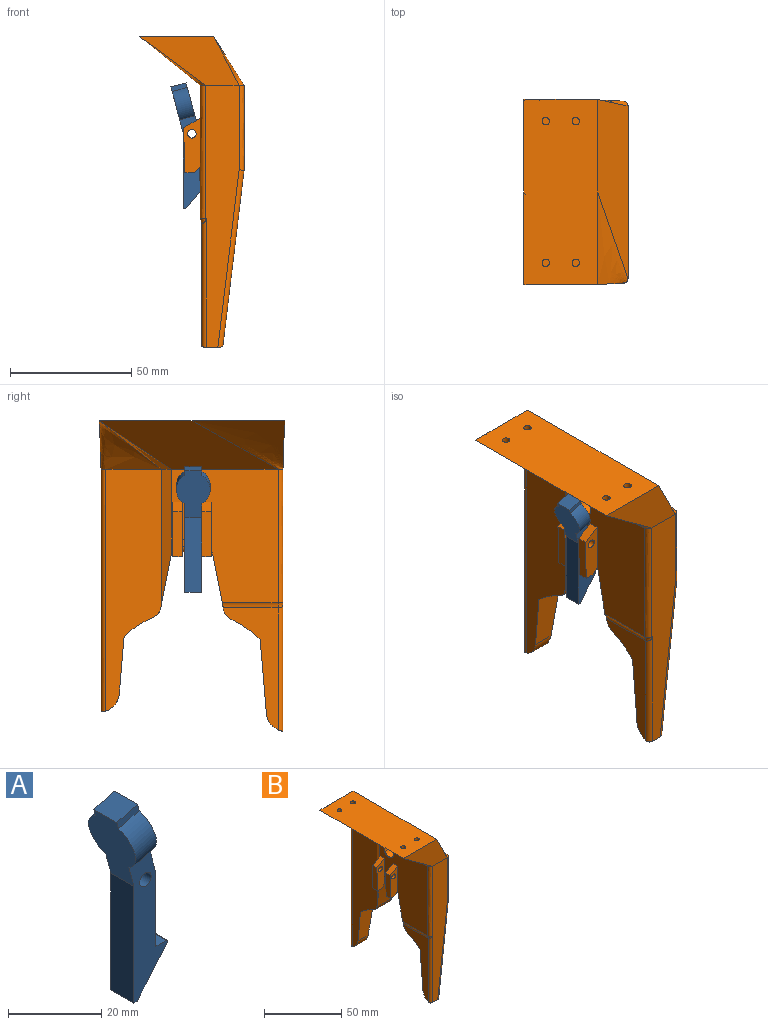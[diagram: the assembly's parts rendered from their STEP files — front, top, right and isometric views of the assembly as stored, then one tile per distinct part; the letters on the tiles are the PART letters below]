
ASSEMBLY  parts=2 mates=1
PART A: 18 faces, bbox 15.4x14x51.8 mm
  f0: plane 6.78x3.55mm, normal (0,-1,0), area 12.6mm2, adj f2,f3,f4,f14
  f1: plane 6.78x3.55mm, normal (0,1,0), area 12.6mm2, adj f2,f3,f4,f13
  f2: plane 20.89x14mm, normal (0.97,0,0.26), area 153.5mm2, adj f0,f1,f3,f9,f11,f12,f13,f14
  f3: plane 7x6.28mm, normal (-0.26,0,0.97), area 45.5mm2, adj f0,f1,f2,f4
  f4: plane 19.32x14mm, normal (-0.97,0,-0.26), area 200.2mm2, adj f0,f1,f3,f5,f11,f12,f13,f14
  f5: plane 30.76x7mm, normal (-1,0,0), area 215.3mm2, adj f4,f6,f11,f12
  f6: plane 7x1mm, normal (0,0,-1), area 7mm2, adj f5,f7,f11,f12
  f7: plane 10.9x9.15mm, normal (0.77,0,-0.64), area 99.6mm2, adj f6,f11,f12,f17
  f8: plane 7x3.14mm, normal (0,0,1), area 22mm2, adj f9,f11,f12,f17
  f9: plane 19.31x7mm, normal (1,0,0), area 135.2mm2, adj f2,f8,f11,f12
  f10: cylinder r=1.75mm len=7mm, axis (0,1,0), area 77mm2, adj f11,f12
  f11: plane 38.18x11.78mm, normal (0,-1,0), area 230.7mm2, adj f2,f4,f5,f6,f7,f8,f9,f10
  f12: plane 38.18x11.78mm, normal (0,1,0), area 230.7mm2, adj f2,f4,f5,f6,f7,f8,f9,f10
  f13: cylinder r=7mm len=13.39mm, axis (-0.97,0,-0.26), area 95.3mm2, adj f1,f2,f4,f12
  f14: cylinder r=7mm len=13.39mm, axis (-0.97,0,-0.26), area 95.3mm2, adj f0,f2,f4,f11
  f15: cylinder r=4.3mm len=9.68mm, axis (0.97,0,0.26), area 143.2mm2, adj f2,f16
  f16: plane 8.6x8.31mm, normal (0.97,0,0.26), area 58.1mm2, adj f15
  f17: cylinder r=0.4mm len=7mm, axis (0,1,0), area 6.4mm2, adj f7,f8,f11,f12
PART B: 79 faces, bbox 43.3x76.8x128.6 mm
  f0: plane 76.8x30.8mm, normal (0,0,1), area 2292.4mm2, adj f62,f63,f64,f65,f66,f67,f68,f69
  f1: plane 100x12mm, normal (0,1,0), area 945.1mm2, adj f14,f19,f21,f32,f69
  f2: plane 22.32x18mm, normal (0,-0.98,-0.2), area 354.1mm2, adj f10,f11,f13,f17,f23
  f3: plane 108x14mm, normal (0,-1,0), area 1164.1mm2, adj f15,f20,f22,f24,f33,f56,f65
  f4: plane 23.76x11.92mm, normal (0,-1,-0.08), area 250.3mm2, adj f7,f10,f17,f21
  f5: plane 30.61x13.28mm, normal (0,1,-0.08), area 351.3mm2, adj f8,f9,f18,f22
  f6: plane 23.29x18.01mm, normal (0,0.98,-0.2), area 392.8mm2, adj f9,f11,f12,f16,f18,f54
  f7: cylinder r=40.5mm len=12.88mm, axis (-1,0,0), area 180.7mm2, adj f4,f10,f13,f17
  f8: cylinder r=39.7mm len=14.27mm, axis (-1,0,0), area 202.7mm2, adj f5,f9,f12,f18
  f9: plane 72.6x27.16mm, normal (0.99,0,-0.12), area 972.1mm2, adj f5,f6,f8,f12,f15,f22,f31
  f10: plane 64.83x27.2mm, normal (0.99,0,-0.12), area 920.9mm2, adj f2,f4,f7,f13,f14,f21,f31
  f11: cylinder r=8.67mm len=18.1mm, axis (-1,0,0), area 365.3mm2, adj f2,f6,f16,f25,f26,f27,f28,f29
  f12: cylinder r=5mm len=14.7mm, axis (-1,0,0), area 69.4mm2, adj f6,f8,f9,f18
  f13: cylinder r=5mm len=13.32mm, axis (-1,0,0), area 63.5mm2, adj f2,f7,f10,f17
  f14: cylinder r=2mm len=65.48mm, axis (-0.12,0,-0.99), area 205.3mm2, adj f1,f10,f21,f32
  f15: cylinder r=2mm len=73.48mm, axis (0.12,0,0.99), area 230.3mm2, adj f3,f9,f22,f33
  f16: plane 55x44mm, normal (-1,0,0), area 1755.9mm2, adj f6,f11,f23,f24,f40,f41,f42,f48
  f17: plane 99.62x23mm, normal (-1,0,0), area 1679.2mm2, adj f2,f4,f7,f13,f19,f21,f23,f70
  f18: plane 50.26x22.56mm, normal (-1,0,0), area 415.4mm2, adj f5,f6,f8,f12,f20,f22,f54
  f19: cylinder r=2mm len=100mm, axis (0,0,1), area 313.6mm2, adj f1,f17,f21,f70
  f20: cylinder r=2mm len=53mm, axis (0,0,-1), area 160.5mm2, adj f3,f18,f22,f55,f56
  f21: cylinder r=8mm len=9.07mm, axis (1,0,0), area 93.8mm2, adj f1,f4,f10,f14,f17,f19
  f22: cylinder r=8mm len=9.6mm, axis (1,0,0), area 93.6mm2, adj f3,f5,f9,f15,f18,f20
  f23: plane 55x4mm, normal (-0.89,0.45,0), area 201.2mm2, adj f2,f16,f17,f62
  f24: cylinder r=2mm len=55mm, axis (0,0,-1), area 172.8mm2, adj f3,f16,f55,f64
  f25: plane 4.75x1.5mm, normal (0,0,-1), area 7.1mm2, adj f11,f31,f34,f35
  f26: plane 5.8x3.87mm, normal (-1,0,0), area 14.7mm2, adj f11,f27,f35
  f27: plane 3.87x3.5mm, normal (0,1,0), area 13.5mm2, adj f11,f26,f31,f34
  f28: plane 3.87x3.5mm, normal (0,-1,0), area 13.5mm2, adj f11,f29,f31,f37
  f29: plane 5.8x3.87mm, normal (-1,0,0), area 14.7mm2, adj f11,f28,f36
  f30: plane 4.75x1.5mm, normal (0,0,-1), area 7.1mm2, adj f11,f31,f36,f37
  f31: plane 71x35mm, normal (1,0,0), area 2448.8mm2, adj f9,f10,f11,f25,f27,f28,f30,f32
  f32: cylinder r=2mm len=35mm, axis (0,0,1), area 109.8mm2, adj f1,f14,f31,f68
  f33: cylinder r=2mm len=35mm, axis (0,0,-1), area 109.8mm2, adj f3,f15,f31,f66
  f34: cylinder r=2mm len=3.5mm, axis (1,0,0), area 7.9mm2, adj f25,f27,f31,f35
  f35: cylinder r=2mm len=6.75mm, axis (0,1,0), area 16.6mm2, adj f11,f25,f26,f34
  f36: cylinder r=2mm len=6.75mm, axis (0,1,0), area 16.6mm2, adj f11,f29,f30,f37
  f37: cylinder r=2mm len=3.5mm, axis (-1,0,0), area 7.9mm2, adj f28,f30,f31,f36
  f38: plane 4x2.49mm, normal (0.73,0,-0.69), area 13.7mm2, adj f39,f40,f41,f44
  f39: plane 4.51x4mm, normal (1,0,0.03), area 11.4mm2, adj f11,f38,f40,f41
  f40: plane 22.48x6.91mm, normal (0,-1,0), area 124.5mm2, adj f11,f16,f38,f39,f42,f43,f44,f45
  f41: plane 22.48x6.91mm, normal (0,1,0), area 124.3mm2, adj f11,f16,f38,f39,f42,f43,f44,f45
  f42: plane 6.9x4mm, normal (-0.5,0,0.87), area 31.9mm2, adj f16,f40,f41,f43
  f43: plane 18.5x4mm, normal (-1,0,-0.03), area 74mm2, adj f40,f41,f42,f44
  f44: plane 4.08x4mm, normal (0,0,-1), area 16.3mm2, adj f38,f40,f41,f43
  f45: cylinder r=1.75mm len=4mm, axis (0,1,0), area 44mm2, adj f40,f41
  f46: plane 4x2.49mm, normal (0.73,0,-0.69), area 13.7mm2, adj f47,f48,f49,f52
  f47: plane 4.51x4mm, normal (1,0,0.03), area 11.4mm2, adj f11,f46,f48,f49
  f48: plane 22.48x6.91mm, normal (0,1,0), area 124.5mm2, adj f11,f16,f46,f47,f50,f51,f52,f53
  f49: plane 22.48x6.91mm, normal (0,-1,0), area 124.3mm2, adj f11,f16,f46,f47,f50,f51,f52,f53
  f50: plane 6.9x4mm, normal (-0.5,0,0.87), area 31.9mm2, adj f16,f48,f49,f51
  f51: plane 18.5x4mm, normal (-1,0,-0.03), area 74mm2, adj f48,f49,f50,f52
  f52: plane 4.08x4mm, normal (0,0,-1), area 16.3mm2, adj f46,f48,f49,f51
  f53: cylinder r=1.75mm len=4mm, axis (0,-1,0), area 44mm2, adj f48,f49
  f54: cylinder r=5mm len=23mm, axis (0,1,0), area 51.4mm2, adj f6,f16,f18,f55
  f55: bspline ~2.43x2.34mm, area 5.6mm2, adj f20,f24,f54,f56
  f56: bspline ~1.49x1.26mm, area 0.1mm2, adj f3,f20,f55
  f57: plane 8.6x5.75mm, normal (-1,0,0), area 9.6mm2, adj f58,f59
  f58: cylinder r=4.3mm len=8.6mm, axis (-1,0,0), area 95.8mm2, adj f16,f57,f59,f61
  f59: cylinder r=4.1mm len=8.2mm, axis (-1,0,0), area 63mm2, adj f57,f58,f60,f61
  f60: plane 8.2x8.2mm, normal (-1,0,0), area 52.8mm2, adj f59
  f61: plane 8.1x3.45mm, normal (1,0,0), area 4.3mm2, adj f58,f59
  f62: bspline ~29.7x26.9mm, area 184.4mm2, adj f0,f23,f63,f70
  f63: plane 73.7x24.9mm, normal (-0.63,0,-0.78), area 1312.6mm2, adj f0,f16,f62,f64
  f64: bspline ~76.4x26.9mm, area 645.4mm2, adj f0,f24,f63,f65
  f65: plane 40.9x20mm, normal (0,-1,-0.03), area 444.3mm2, adj f0,f3,f64,f66
  f66: bspline ~76.4x20mm, area 475.9mm2, adj f0,f33,f65,f67
  f67: plane 73.7x20mm, normal (0.85,0,0.53), area 1287.7mm2, adj f0,f31,f66,f68
  f68: bspline ~24.86x20mm, area 88mm2, adj f0,f32,f67,f69
  f69: plane 22.66x20mm, normal (0,1,-0.03), area 180.9mm2, adj f0,f1,f68,f70
  f70: bspline ~35.02x25.7mm, area 446.8mm2, adj f0,f17,f19,f62,f69
  f71: cylinder r=1.55mm len=5mm, axis (0,0,1), area 48.7mm2, adj f0,f72
  f72: plane 3.1x3.1mm, normal (0,0,1), area 7.5mm2, adj f71
  f73: cylinder r=1.55mm len=5mm, axis (0,0,1), area 48.7mm2, adj f0,f74
  f74: plane 3.1x3.1mm, normal (0,0,1), area 7.5mm2, adj f73
  f75: cylinder r=1.55mm len=5mm, axis (0,0,1), area 48.7mm2, adj f0,f76
  f76: plane 3.1x3.1mm, normal (0,0,1), area 7.5mm2, adj f75
  f77: cylinder r=1.55mm len=5mm, axis (0,0,1), area 48.7mm2, adj f0,f78
  f78: plane 3.1x3.1mm, normal (0,0,1), area 7.5mm2, adj f77
PLACE A t=(-31.23,-20.26,-14.65)mm
PLACE B t=(-31.23,-19.76,-14.65)mm fixed
MATE revolute A.f10 <-> B.f45  axis (0,-1,0) through (-33.23,-23.76,25.35)mm
